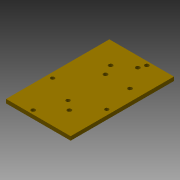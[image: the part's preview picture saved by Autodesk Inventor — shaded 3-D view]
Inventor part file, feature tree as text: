
AUTODESK INVENTOR PART (.ipt)
format: ipt  version: 2013 SP2 (Build 170200200, 200)  size: 100,352 bytes
history: native  units: mm
features: reference x9, extrude x2, sketch x2
ambient origin geometry x8: Origin, YZ Plane, XZ Plane, XY Plane, X Axis, Y Axis, Z Axis, Center Point
bodies: Solid1 (feature_tree)
feature tree (13):
  extrude  "Extrusion1"  Depth=3.0mm
  extrude  "Extrusion2"  Depth=5.0mm TaperAngle=0.0deg
  sketch  "Sketch1"  dims[d0=50.0mm d1=3.0mm]
  sketch  "Sketch2"  dims[d2=80.0mm d3=0.0mm d10=5.0mm d11=0.0mm d13=10.0mm d14=10.0mm d15=30.0mm d16=3.0mm d17=23.0mm]
  reference  "Reference1"
  reference  "Reference2"
  reference  "Reference25"
  reference  "Reference26"
  reference  "Reference27"
  reference  "Reference28"
  reference  "Reference29"
  reference  "Reference30"
  reference  "Reference31"
